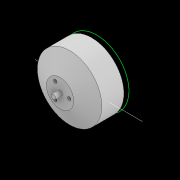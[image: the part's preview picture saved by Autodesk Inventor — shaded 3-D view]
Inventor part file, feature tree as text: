
AUTODESK INVENTOR PART (.ipt)
format: ipt  version: 2022.2 (Build 262287010, 287A)  size: 176,128 bytes
history: native  units: mm
features: sketch x9, extrude x5, hole x3, chamfer x2
ambient origin geometry x8: Origin, YZ Plane, XZ Plane, XY Plane, X Axis, Y Axis, Z Axis, Center Point
bodies: Solid1 (feature_tree)
feature tree (19):
  sketch  "Sketch1"  dims[d0=59.0mm d1=32.0mm]
  extrude  "Extrusion1"  Depth=32.0mm
  extrude  "Extrusion2"  Depth=17.0mm
  extrude  "Extrusion3"  Depth=40.0mm TaperAngle=360.0deg
  hole  "Hole1"  [1 undecoded]
  chamfer  "Chamfer1"  Distance=42.5mm
  extrude  "Magnet"  Depth=3.0mm TaperAngle=0.0deg
  chamfer  "Chamfer2"  Distance=25.0mm
  sketch  "Sketch7"  dims[d22=3.0mm]
  hole  "Hole2"  [1 undecoded]
  hole  "Hole3"  [1 undecoded]
  extrude  "Extrusion5"  Depth=4.5mm TaperAngle=45.0deg
  sketch  "Sketch9"  dims[d28=20.594885mm d29=25.0mm d30=8.8mm d31=17.0mm d32=45.0deg d33=2.0mm d34=0.0mm d35=4.5mm d36=7.5mm d37=45.0deg d38=3.0mm d39=6.0mm d40=4.0mm d41=2.0mm d42=90.0deg d43=4.0mm d44=20.594885mm d45=2.5mm d46=6.0mm d47=4.0mm d48=2.0mm d49=90.0deg d50=3.0mm d51=20.594885mm d52=0.5mm d53=0.0mm]
  sketch  "Sketch2"  dims[d2=25.0mm d3=17.0mm]
  sketch  "Sketch3"  dims[d4=45.0deg d6=40.0mm d8=360.0deg]
  sketch  "Sketch4"  dims[d10=30.0mm d12=360.0deg d14=6.0mm]
  sketch  "Sketch5"  dims[d15=4.0mm d16=42.5mm d17=0.0mm]
  sketch  "Sketch6"  dims[d18=6.0mm d19=0.0mm d20=3.0mm d21=0.0mm]
  sketch  "Sketch8"  dims[d23=6.0mm d24=4.0mm d25=2.0mm d26=90.0deg d27=5.0mm]
note: 3 required parameter values undecoded (feature->parameter linkage not recoverable at this tier; creation-order binding heuristic only, values carry confidence <= 0.55)
